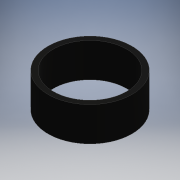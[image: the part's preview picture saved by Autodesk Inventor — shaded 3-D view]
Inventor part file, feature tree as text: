
AUTODESK INVENTOR PART (.ipt)
format: ipt  version: 2020.2 (Build 242310000, 310)  size: 95,232 bytes
history: native  units: mm
features: other x1, sketch x1, extrude x1
ambient origin geometry x8: Origin, YZ Plane, XZ Plane, XY Plane, X Axis, Y Axis, Z Axis, Center Point
bodies: Body1 (feature_tree)
feature tree (3):
  other  "ソリッド1"
  sketch  "スケッチ1"
  extrude  "押し出し1"  Depth=14.0mm
